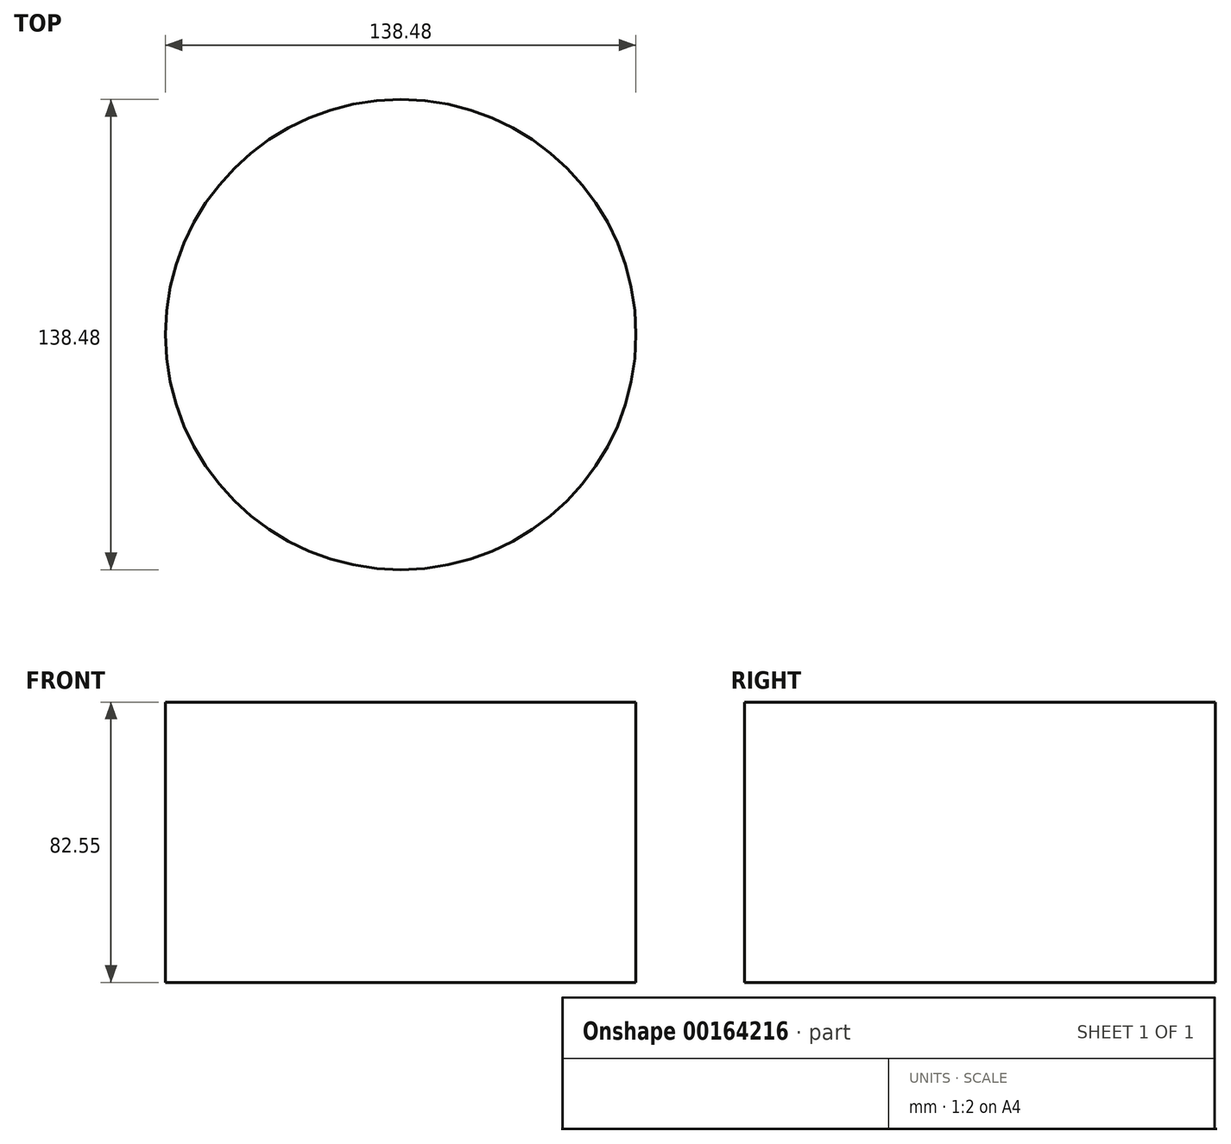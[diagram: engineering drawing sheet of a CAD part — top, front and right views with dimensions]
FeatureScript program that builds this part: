
annotation { "Feature Type Name" : "Feature", "Feature Type Description" : "" }
export const myFeature = defineFeature(function(context is Context, id is Id, definition is map)
    precondition{}
    {
        {
            var Q0;
            Q0=qCreatedBy(makeId("Top.planeOp"),FACE);
            var sketch = newSketch(context, id + "F0", { "sketchPlane" : qUnion([Q0])});
            skCircle(sketch, "E0", {"center": v(0, 0) * mm, "radius": 69.24 * mm});
            skSolve(sketch);
        }
        {
            var Q0;
            Q0 = qSketchRegion(id + "F0", true);
            var Q1;
            Q1=makeQuery(id+"F0.imprint","IMPRINT",FACE,{"disambiguationData":[TD([[makeQuery(id+"F0.imprint","IMPRINT",EDGE,{"derivedFrom":sQuery(id+"F0.wireOp",EDGE,"E0")}),1.0]])]});
            extrude(context, id + "F1", {"entities" : qUnion([Q0, Q1]), "depth" : 82.55 * mm});
        }
    });
